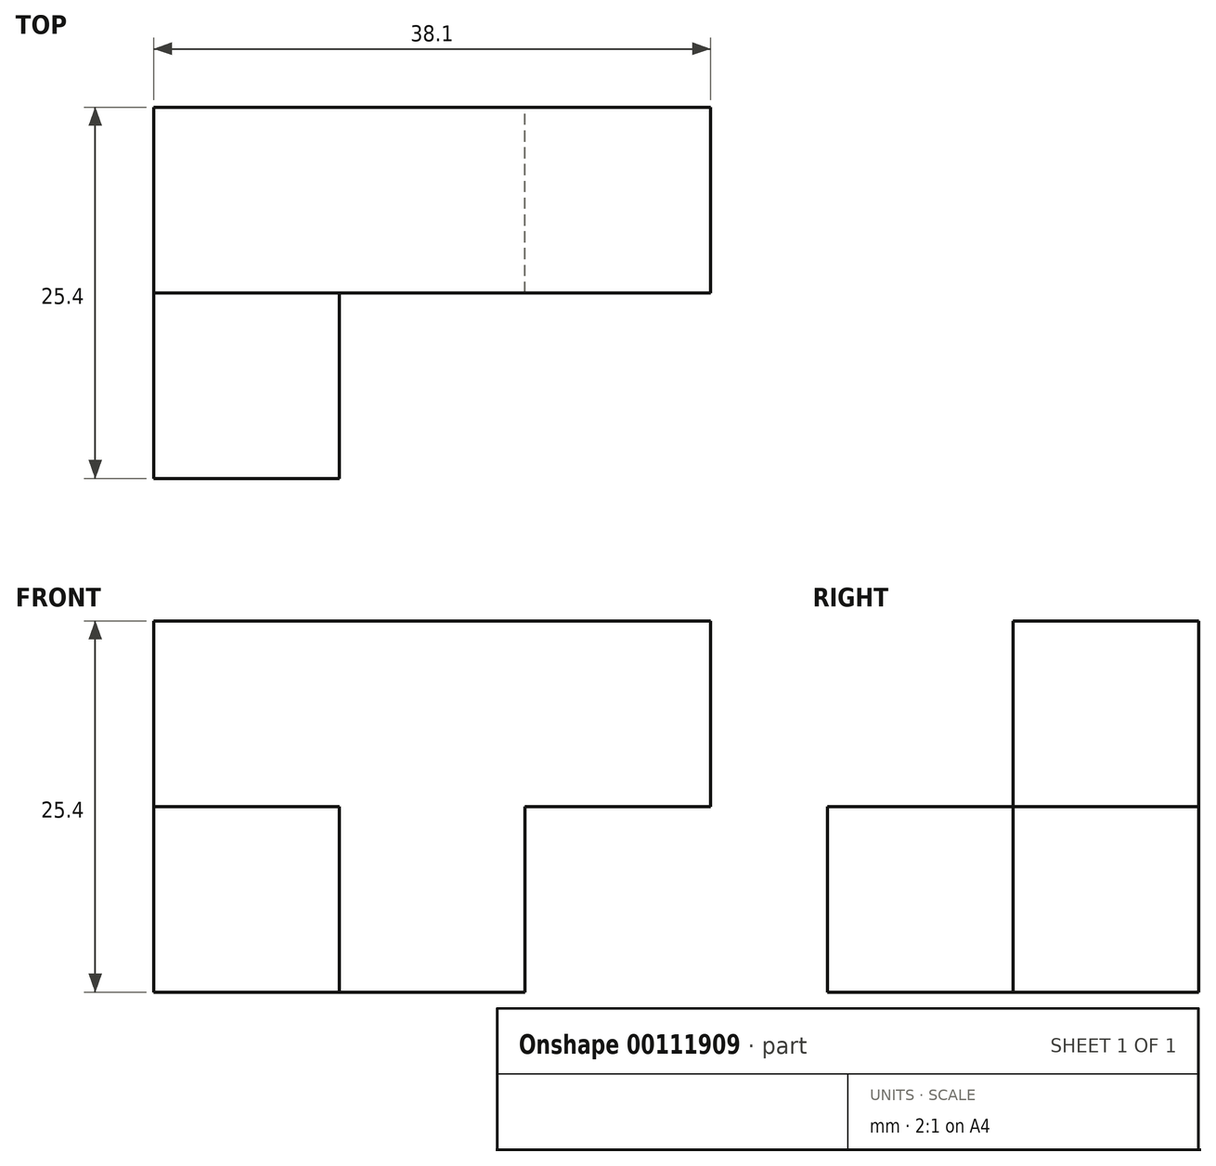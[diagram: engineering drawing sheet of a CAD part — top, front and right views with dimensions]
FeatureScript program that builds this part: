
annotation { "Feature Type Name" : "Feature", "Feature Type Description" : "" }
export const myFeature = defineFeature(function(context is Context, id is Id, definition is map)
    precondition{}
    {
        {
            var Q0;
            Q0=qCreatedBy(makeId("Front.planeOp"),FACE);
            var sketch = newSketch(context, id + "F0", { "sketchPlane" : qUnion([Q0])});
            skLineSegment(sketch, "E0.bottom", {"start": v(-22.71, 7.67) * mm, "end": v(15.39, 7.67) * mm});
            skLineSegment(sketch, "E0.top", {"start": v(-22.71, -5.03) * mm, "end": v(15.39, -5.03) * mm});
            skLineSegment(sketch, "E0.left", {"start": v(-22.71, 7.67) * mm, "end": v(-22.71, -5.03) * mm});
            skLineSegment(sketch, "E0.right", {"start": v(15.39, 7.67) * mm, "end": v(15.39, -5.03) * mm});
            skSolve(sketch);
        }
        {
            var Q0;
            Q0=makeQuery(id+"F0.imprint","IMPRINT",FACE,{"disambiguationData":[TD([[makeQuery(id+"F0.imprint","IMPRINT",EDGE,{"derivedFrom":sQuery(id+"F0.wireOp",EDGE,"E0.bottom")}),-1.0]])]});
            extrude(context, id + "F1", {"entities" : qUnion([Q0]), "depth" : 12.7 * mm});
        }
        {
            var Q0;
            Q0=makeQuery(id+"F1.opExtrude","SWEPT_FACE",FACE,{"disambiguationData":[OSD([sQuery(id+"F0.wireOp",EDGE,"E0.top")])]});
            var sketch = newSketch(context, id + "F2", { "sketchPlane" : qUnion([Q0])});
            skLineSegment(sketch, "E1", {"start": v(15.39, 12.7) * mm, "end": v(2.69, 12.7) * mm});
            skLineSegment(sketch, "E2", {"start": v(2.69, 12.7) * mm, "end": v(2.69, 0) * mm});
            skSolve(sketch);
        }
        {
            var Q0;
            Q0 = qSketchRegion(id + "F2", true);
            var Q1;
            {var subQ0=sQuery(id+"F2.wireOp",EDGE,"E2");Q1=makeQuery(id+"F2.imprint","IMPRINT",FACE,{"disambiguationData":[TD([[makeQuery(id+"F2.imprint","IMPRINT",EDGE,{"derivedFrom":subQ0}),-1.0]])]});}
            extrude(context, id + "F3", {"entities" : qUnion([Q0, Q1]), "operationType" : NewBodyOperationType.ADD, "depth" : 12.7 * mm});
        }
        {
            var Q0;
            {var subQ0=sQuery(id+"F0.wireOp",EDGE,"E0.top");var subQ1=makeQuery(id+"F1.opExtrude","CAP_EDGE",EDGE,{"disambiguationData":[OSD([subQ0])],"isStart":false});var subQ2=sQuery(id+"F0.wireOp",EDGE,"E0.left");Q0=makeQuery(id+"F3.boolean.opBoolean","MERGE",FACE,{"derivedFrom":[makeQuery(id+"F1.opExtrude","CAP_FACE",FACE,{"disambiguationData":[OSD([sQuery(id+"F0.wireOp",EDGE,"E0.bottom"),subQ0,subQ2,sQuery(id+"F0.wireOp",EDGE,"E0.right")])],"isStart":false}),makeQuery(id+"F3.opExtrude","SWEPT_FACE",FACE,{"disambiguationData":[OSD([subQ0]),TDD([makeQuery(id+"F2.imprint","IMPRINT",EDGE,{"disambiguationData":[TD([[makeQuery(id+"F2.imprint","INTERSECT",VERTEX,{"derivedFrom":[makeQuery(id+"F1.opExtrude","SWEPT_EDGE",EDGE,{"disambiguationData":[OSD([subQ0,subQ2])]}),subQ1]}),-1.0]])],"derivedFrom":subQ1})])]})]});}
            var sketch = newSketch(context, id + "F4", { "sketchPlane" : qUnion([Q0])});
            skLineSegment(sketch, "E3", {"start": v(-22.71, -17.73) * mm, "end": v(-10.01, -17.73) * mm});
            skLineSegment(sketch, "E4", {"start": v(-10.01, -17.73) * mm, "end": v(-10.01, -5.03) * mm});
            skLineSegment(sketch, "E5", {"start": v(-10.01, -5.03) * mm, "end": v(-22.71, -5.03) * mm});
            skSolve(sketch);
        }
        {
            var Q0;
            Q0 = qSketchRegion(id + "F4", true);
            var Q1;
            {var subQ0=sQuery(id+"F4.wireOp",EDGE,"E3");Q1=makeQuery(id+"F4.imprint","IMPRINT",FACE,{"disambiguationData":[TD([[makeQuery(id+"F4.imprint","IMPRINT",EDGE,{"derivedFrom":subQ0}),1.0]])]});}
            extrude(context, id + "F5", {"entities" : qUnion([Q0, Q1]), "operationType" : NewBodyOperationType.ADD, "depth" : 12.7 * mm});
        }
    });
